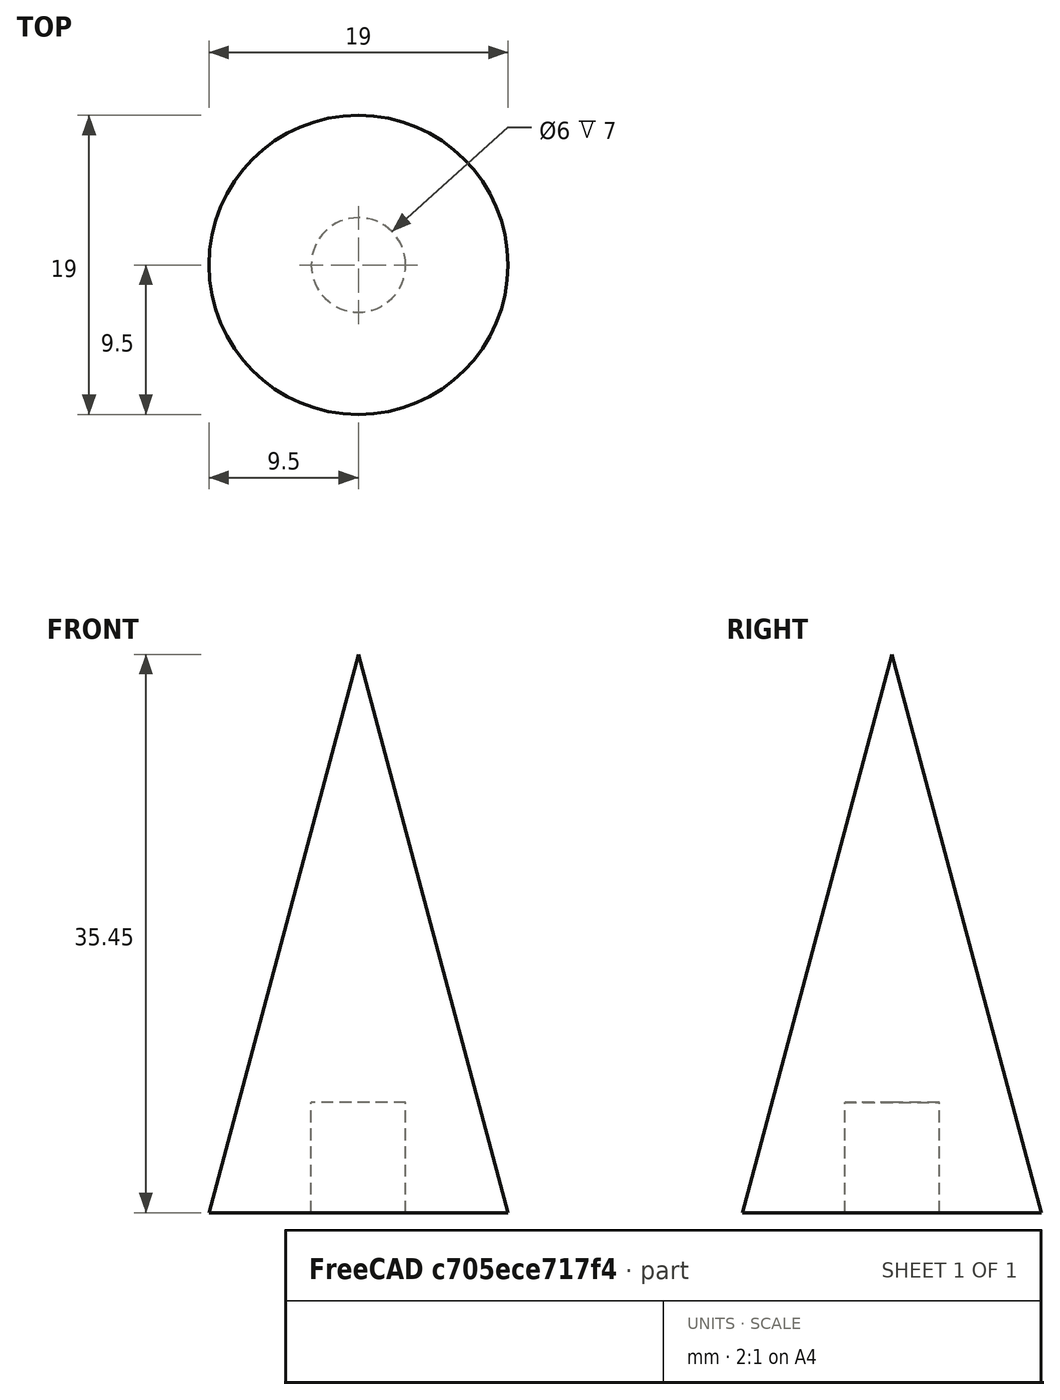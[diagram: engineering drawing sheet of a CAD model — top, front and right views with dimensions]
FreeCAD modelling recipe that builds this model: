
FCSTD DOCUMENT  (FreeCAD 0.19R24291 (Git))
Label: windDirectionArrowTopv2
License: All rights reserved
LicenseURL: http://en.wikipedia.org/wiki/All_rights_reserved
objects: Sketcher::SketchObject×1, PartDesign::Revolution×1, PartDesign::Body×1
note: 4 computed .brp shape members not serialized (recipe doc carries the construction recipe); baked Part::Feature solids carry a one-line shape summary decoded from their .brp

FEATURE [Sketcher::SketchObject] Sketch
  FullyConstrained = true
  MapMode = 5
  Placement = pos=(0,0,0) rot=(1,0,0;1.5708rad)
  Support = -> [XZ_Plane]
  sketch-geometry (5):
    g0: LineSegment StartX=3 StartY=0 StartZ=0 EndX=9.5 EndY=0 EndZ=0
    g1: LineSegment StartX=9.5 StartY=0 StartZ=0 EndX=0 EndY=35.4545 EndZ=0
    g2: LineSegment StartX=3 StartY=0 StartZ=0 EndX=3 EndY=7 EndZ=0
    g3: LineSegment StartX=3 StartY=7 StartZ=0 EndX=0 EndY=7 EndZ=0
    g4: LineSegment StartX=0 StartY=35.4545 StartZ=0 EndX=0 EndY=7 EndZ=0
  constraints (15):
    c: PointOnObject(g0,g-1)
    c: Horizontal(g0)
    c: Coincident(g1,g0)
    c: DistanceX(g-1,g0) = 3
    c: Angle(g1,g0) = 1.309
    c: DistanceX(g0,g0) = 6.5
    c: PointOnObject(g1,g-2)
    c: Coincident(g2,g0)
    c: Vertical(g2)
    c: Coincident(g3,g2)
    c: Horizontal(g3)
    c: PointOnObject(g3,g-2)
    c: DistanceY(g2,g2) = 7
    c: Coincident(g4,g1)
    c: Coincident(g4,g3)
FEATURE [PartDesign::Revolution] Revolution
  Angle = 360
  Axis = (0,-2e-16,1)
  Base = (0,0,0)
  Placement = pos=(0,0,0) rot=(1,0,0;1.5708rad)
  Profile = -> Sketch
  ReferenceAxis = -> Sketch [V_Axis]
  Reversed = true
FEATURE [PartDesign::Body] Body
  Group = -> [Sketch,Revolution]
  Origin = -> Origin
  Tip = -> Revolution
